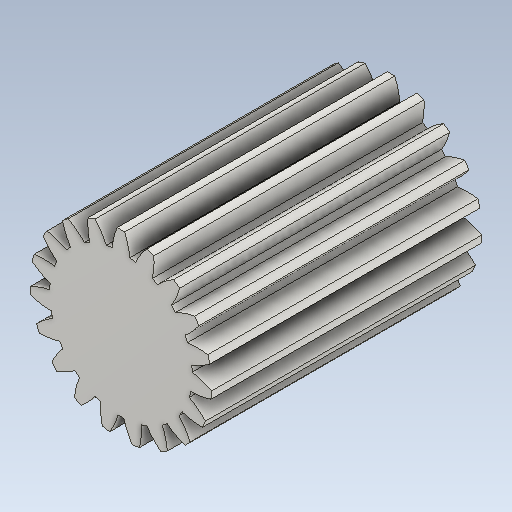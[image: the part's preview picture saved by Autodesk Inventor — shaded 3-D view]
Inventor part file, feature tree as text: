
AUTODESK INVENTOR PART (.ipt)
format: ipt  version: 2021 (Build 250183000, 183)  size: 286,720 bytes
history: native  units: mm (DEFAULTED — no unit token found)
features: plane x3, other x3, sketch x2, extrude x1
ambient origin geometry x8: Origin, YZ Plane, XZ Plane, XY Plane, X Axis, Y Axis, Z Axis, Center Point
bodies: Solid1 (feature_tree)
feature tree (9):
  extrude  "Extrusion1"  Depth=5.0mm TaperAngle=0.0deg
  plane  "Work Plane2"
  plane  "Work Plane8"
  plane  "Work Plane9"
  other  "Spur Gear"
  sketch  "Sketch1"  dims[d0=3.356446mm d1=5.0mm d2=0.0mm]
  sketch  "Sketch2"  dims[d3=3.04mm d4=10.0mm d5=0.0mm d16=7.5mm d17=0.0mm d34=1.65347mm d39=0.0mm d41=0.0mm d43=7.5mm d46=7.5mm d47=0.0mm d48=0.0mm]
  other  "Srf1"
  other  "Pitch Diameter"
